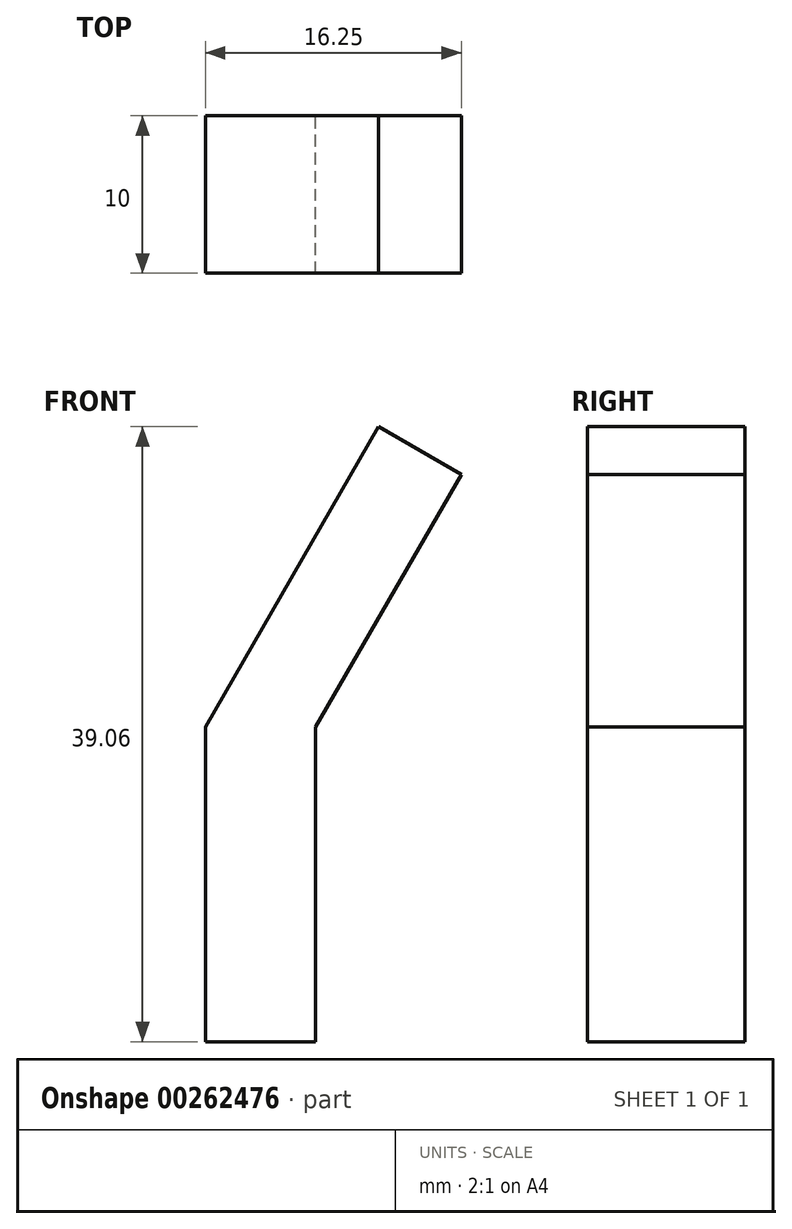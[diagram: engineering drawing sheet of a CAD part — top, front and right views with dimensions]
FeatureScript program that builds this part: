
annotation { "Feature Type Name" : "Feature", "Feature Type Description" : "" }
export const myFeature = defineFeature(function(context is Context, id is Id, definition is map)
    precondition{}
    {
        {
            var Q0;
            Q0=qCreatedBy(makeId("Front.planeOp"),FACE);
            var sketch = newSketch(context, id + "F0", { "sketchPlane" : qUnion([Q0])});
            skLineSegment(sketch, "E0", {"start": v(0, 0) * mm, "end": v(0, 20) * mm});
            skLineSegment(sketch, "E1", {"start": v(0, 20) * mm, "end": v(11, 39.06) * mm});
            skLineSegment(sketch, "E2", {"start": v(11, 39.06) * mm, "end": v(16.25, 36.03) * mm});
            skLineSegment(sketch, "E3", {"start": v(16.25, 36.03) * mm, "end": v(7, 20) * mm});
            skLineSegment(sketch, "E4", {"start": v(7, 20) * mm, "end": v(7, 0) * mm});
            skLineSegment(sketch, "E5", {"start": v(7, 0) * mm, "end": v(0, 0) * mm});
            skSolve(sketch);
        }
        {
            var Q0;
            Q0 = qSketchRegion(id + "F0", true);
            extrude(context, id + "F1", {"entities" : qUnion([Q0]), "depth" : 10 * mm});
        }
    });
